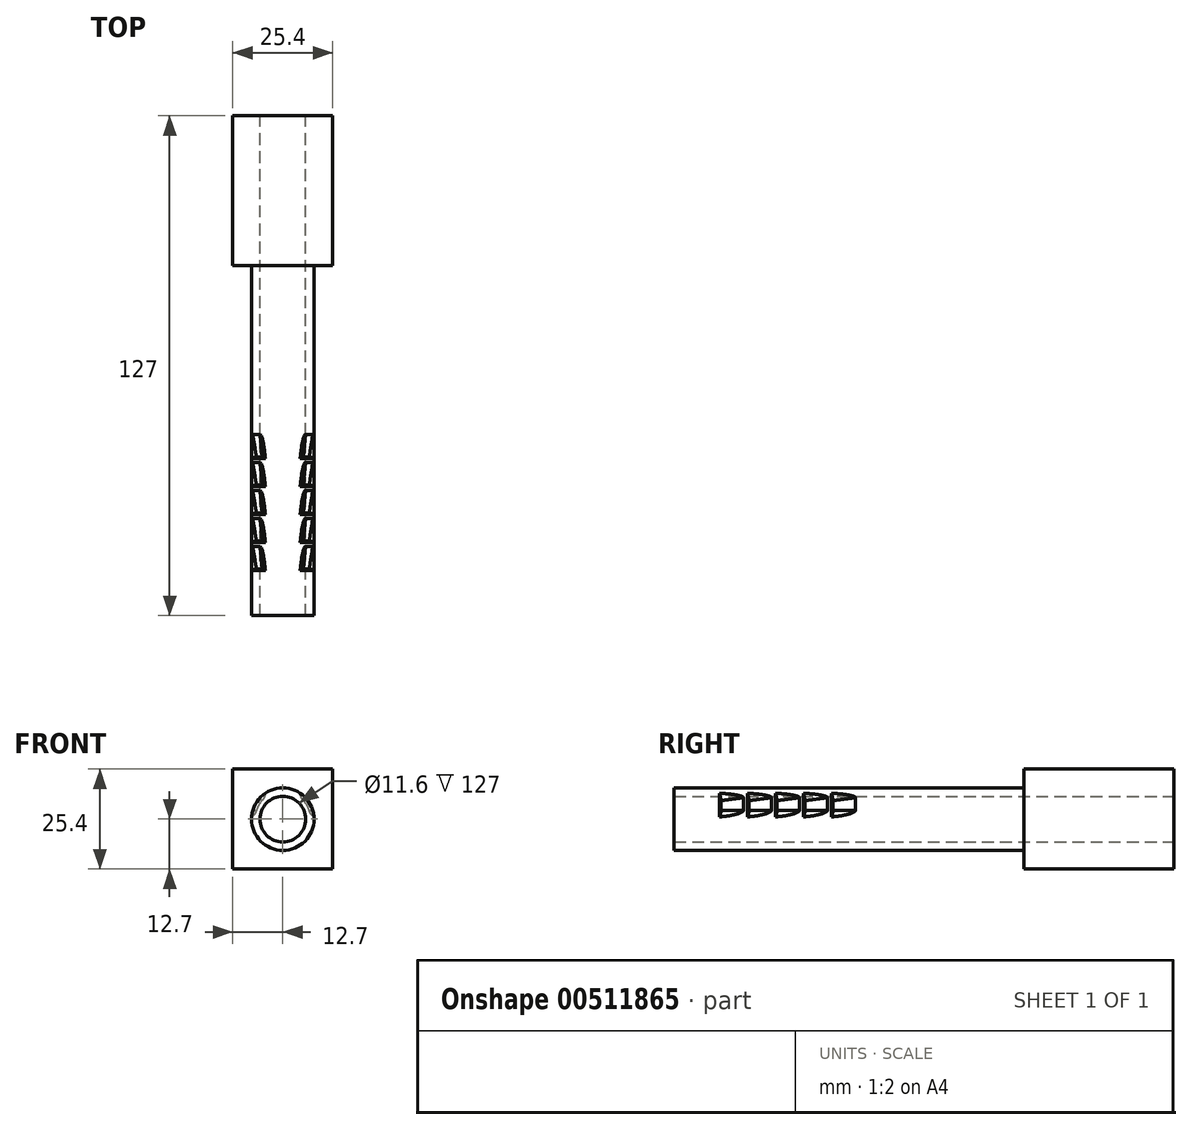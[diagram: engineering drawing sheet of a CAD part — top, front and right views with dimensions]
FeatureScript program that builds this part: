
annotation { "Feature Type Name" : "Feature", "Feature Type Description" : "" }
export const myFeature = defineFeature(function(context is Context, id is Id, definition is map)
    precondition{}
    {
        {
            var Q0;
            Q0=qCreatedBy(makeId("Front.planeOp"),FACE);
            var sketch = newSketch(context, id + "F0", { "sketchPlane" : qUnion([Q0])});
            skLineSegment(sketch, "E0.bottom", {"start": v(12.7, -12.7) * mm, "end": v(-12.7, -12.7) * mm});
            skLineSegment(sketch, "E0.top", {"start": v(12.7, 12.7) * mm, "end": v(-12.7, 12.7) * mm});
            skLineSegment(sketch, "E0.left", {"start": v(12.7, -12.7) * mm, "end": v(12.7, 12.7) * mm});
            skLineSegment(sketch, "E0.right", {"start": v(-12.7, -12.7) * mm, "end": v(-12.7, 12.7) * mm});
            skPoint(sketch, "E0.middle", {"position": v(0, 0) * mm});
            skCircle(sketch, "E1", {"center": v(0, 0) * mm, "radius": 7.94 * mm});
            skCircle(sketch, "E2", {"center": v(0, 0) * mm, "radius": 5.8 * mm});
            skSolve(sketch);
        }
        {
            var Q0;
            Q0=qSketchRegion(id+"F0",true);
            var Q1;
            Q1=makeQuery(id+"F0.imprint","IMPRINT",FACE,{"disambiguationData":[TD([[makeQuery(id+"F0.imprint","IMPRINT",EDGE,{"derivedFrom":sQuery(id+"F0.wireOp",EDGE,"E1")}),1.0]])]});
            extrude(context, id + "F1", {"entities" : qUnion([Q0, Q1]), "depth" : 38.1 * mm});
        }
        {
            var Q0;
            Q0=makeQuery(id+"F0.imprint","IMPRINT",FACE,{"disambiguationData":[TD([[makeQuery(id+"F0.imprint","IMPRINT",EDGE,{"derivedFrom":sQuery(id+"F0.wireOp",EDGE,"E1")}),1.0]])]});
            extrude(context, id + "F2", {"entities" : qUnion([Q0]), "operationType" : NewBodyOperationType.ADD, "depth" : 127 * mm, "offsetDistance" : 25.4 * mm});
        }
        {
            var Q0;
            Q0=qCreatedBy(makeId("Top.planeOp"),FACE);
            var sketch = newSketch(context, id + "F3", { "sketchPlane" : qUnion([Q0])});
            skLineSegment(sketch, "E3", {"start": v(-8.1, -115.62) * mm, "end": v(-7.07, -115.1) * mm});
            skLineSegment(sketch, "E4", {"start": v(-7.07, -115.1) * mm, "end": v(-8.03, -108.82) * mm});
            skLineSegment(sketch, "E5", {"start": v(-8.03, -108.82) * mm, "end": v(-8.1, -115.62) * mm});
            skLineSegment(sketch, "E6.0.1.0", {"start": v(-8.03, -101.7) * mm, "end": v(-8.1, -108.5) * mm});
            skLineSegment(sketch, "E6.0.1.1", {"start": v(-7.07, -108) * mm, "end": v(-8.03, -101.7) * mm});
            skLineSegment(sketch, "E6.0.1.2", {"start": v(-8.1, -108.5) * mm, "end": v(-7.07, -108) * mm});
            skLineSegment(sketch, "E6.0.2.0", {"start": v(-8.03, -94.6) * mm, "end": v(-8.1, -101.4) * mm});
            skLineSegment(sketch, "E6.0.2.1", {"start": v(-7.07, -100.88) * mm, "end": v(-8.03, -94.6) * mm});
            skLineSegment(sketch, "E6.0.2.2", {"start": v(-8.1, -101.4) * mm, "end": v(-7.07, -100.88) * mm});
            skLineSegment(sketch, "E6.0.3.0", {"start": v(-8.03, -87.48) * mm, "end": v(-8.1, -94.28) * mm});
            skLineSegment(sketch, "E6.0.3.1", {"start": v(-7.07, -93.77) * mm, "end": v(-8.03, -87.48) * mm});
            skLineSegment(sketch, "E6.0.3.2", {"start": v(-8.1, -94.28) * mm, "end": v(-7.07, -93.77) * mm});
            skLineSegment(sketch, "E6.0.4.0", {"start": v(-8.03, -80.37) * mm, "end": v(-8.1, -87.17) * mm});
            skLineSegment(sketch, "E6.0.4.1", {"start": v(-7.07, -86.66) * mm, "end": v(-8.03, -80.37) * mm});
            skLineSegment(sketch, "E6.0.4.2", {"start": v(-8.1, -87.17) * mm, "end": v(-7.07, -86.66) * mm});
            skLineSegment(sketch, "E6.direction1", {"start": v(-8.1, -115.62) * mm, "end": v(-0.22, -115.62) * mm, "construction": true});
            skLineSegment(sketch, "E6.direction2", {"start": v(-8.1, -115.62) * mm, "end": v(-8.1, -108.5) * mm, "construction": true});
            skSolve(sketch);
        }
        {
            var Q0;
            Q0 = qSketchRegion(id + "F3", true);
            var Q1;
            Q1=makeQuery(id+"F1.opExtrude","CAP_EDGE",EDGE,{"disambiguationData":[OSD([sQuery(id+"F0.wireOp",EDGE,"E2")])],"isStart":true});
            revolve(context, id + "F4", {"operationType" : NewBodyOperationType.REMOVE, "entities" : qUnion([Q0]), "axis" : qUnion([Q1]), "revolveType" : RevolveType.ONE_DIRECTION, "oppositeDirection" : true, "angle" : 60 * degree});
        }
        {
            var Q0;
            Q0 = qSketchRegion(id + "F3", true);
            var Q1;
            Q1=makeQuery(id+"F2.opExtrude","SWEPT_FACE",FACE,{"disambiguationData":[OSD([sQuery(id+"F0.wireOp",EDGE,"E1")])]});
            revolve(context, id + "F5", {"operationType" : NewBodyOperationType.REMOVE, "entities" : qUnion([Q0]), "axis" : qUnion([Q1]), "revolveType" : RevolveType.TWO_DIRECTIONS, "angle" : 180 * degree, "angleBack" : 120 * degree});
        }
        {
            var Q0;
            Q0=makeQuery(id+"F5.boolean.opBoolean","COPY",EDGE,{"derivedFrom":makeQuery(id+"F5.opRevolve","CAP_EDGE",EDGE,{"disambiguationData":[OSD([sQuery(id+"F3.wireOp",EDGE,"E4")])],"isStart":true})});
            var Q1;
            Q1=makeQuery(id+"F5.boolean.opBoolean","COPY",EDGE,{"derivedFrom":makeQuery(id+"F5.opRevolve","CAP_EDGE",EDGE,{"disambiguationData":[OSD([sQuery(id+"F3.wireOp",EDGE,"E4")])],"isStart":false})});
            var Q2;
            Q2=makeQuery(id+"F5.boolean.opBoolean","COPY",EDGE,{"derivedFrom":makeQuery(id+"F5.opRevolve","CAP_EDGE",EDGE,{"disambiguationData":[OSD([sQuery(id+"F3.wireOp",EDGE,"E6.0.1.1")])],"isStart":true})});
            var Q3;
            Q3=makeQuery(id+"F5.boolean.opBoolean","COPY",EDGE,{"derivedFrom":makeQuery(id+"F5.opRevolve","CAP_EDGE",EDGE,{"disambiguationData":[OSD([sQuery(id+"F3.wireOp",EDGE,"E6.0.1.1")])],"isStart":false})});
            var Q4;
            Q4=makeQuery(id+"F5.boolean.opBoolean","COPY",EDGE,{"derivedFrom":makeQuery(id+"F5.opRevolve","CAP_EDGE",EDGE,{"disambiguationData":[OSD([sQuery(id+"F3.wireOp",EDGE,"E6.0.2.1")])],"isStart":true})});
            var Q5;
            Q5=makeQuery(id+"F5.boolean.opBoolean","COPY",EDGE,{"derivedFrom":makeQuery(id+"F5.opRevolve","CAP_EDGE",EDGE,{"disambiguationData":[OSD([sQuery(id+"F3.wireOp",EDGE,"E6.0.2.1")])],"isStart":false})});
            var Q6;
            Q6=makeQuery(id+"F5.boolean.opBoolean","COPY",EDGE,{"derivedFrom":makeQuery(id+"F5.opRevolve","CAP_EDGE",EDGE,{"disambiguationData":[OSD([sQuery(id+"F3.wireOp",EDGE,"E6.0.3.1")])],"isStart":false})});
            var Q7;
            Q7=makeQuery(id+"F5.boolean.opBoolean","COPY",EDGE,{"derivedFrom":makeQuery(id+"F5.opRevolve","CAP_EDGE",EDGE,{"disambiguationData":[OSD([sQuery(id+"F3.wireOp",EDGE,"E6.0.3.1")])],"isStart":true})});
            var Q8;
            Q8=makeQuery(id+"F5.boolean.opBoolean","COPY",EDGE,{"derivedFrom":makeQuery(id+"F5.opRevolve","CAP_EDGE",EDGE,{"disambiguationData":[OSD([sQuery(id+"F3.wireOp",EDGE,"E6.0.4.1")])],"isStart":true})});
            var Q9;
            Q9=makeQuery(id+"F5.boolean.opBoolean","COPY",EDGE,{"derivedFrom":makeQuery(id+"F5.opRevolve","CAP_EDGE",EDGE,{"disambiguationData":[OSD([sQuery(id+"F3.wireOp",EDGE,"E6.0.4.1")])],"isStart":false})});
            var Q10;
            Q10=makeQuery(id+"F4.boolean.opBoolean","COPY",EDGE,{"derivedFrom":makeQuery(id+"F4.opRevolve","CAP_EDGE",EDGE,{"disambiguationData":[OSD([sQuery(id+"F3.wireOp",EDGE,"E4")])],"isStart":false})});
            var Q11;
            Q11=makeQuery(id+"F4.boolean.opBoolean","COPY",EDGE,{"derivedFrom":makeQuery(id+"F4.opRevolve","CAP_EDGE",EDGE,{"disambiguationData":[OSD([sQuery(id+"F3.wireOp",EDGE,"E4")])],"isStart":true})});
            var Q12;
            Q12=makeQuery(id+"F4.boolean.opBoolean","COPY",EDGE,{"derivedFrom":makeQuery(id+"F4.opRevolve","CAP_EDGE",EDGE,{"disambiguationData":[OSD([sQuery(id+"F3.wireOp",EDGE,"E6.0.1.1")])],"isStart":true})});
            var Q13;
            Q13=makeQuery(id+"F4.boolean.opBoolean","COPY",EDGE,{"derivedFrom":makeQuery(id+"F4.opRevolve","CAP_EDGE",EDGE,{"disambiguationData":[OSD([sQuery(id+"F3.wireOp",EDGE,"E6.0.1.1")])],"isStart":false})});
            var Q14;
            Q14=makeQuery(id+"F4.boolean.opBoolean","COPY",EDGE,{"derivedFrom":makeQuery(id+"F4.opRevolve","CAP_EDGE",EDGE,{"disambiguationData":[OSD([sQuery(id+"F3.wireOp",EDGE,"E6.0.2.1")])],"isStart":false})});
            var Q15;
            Q15=makeQuery(id+"F4.boolean.opBoolean","COPY",EDGE,{"derivedFrom":makeQuery(id+"F4.opRevolve","CAP_EDGE",EDGE,{"disambiguationData":[OSD([sQuery(id+"F3.wireOp",EDGE,"E6.0.2.1")])],"isStart":true})});
            var Q16;
            Q16=makeQuery(id+"F4.boolean.opBoolean","COPY",EDGE,{"derivedFrom":makeQuery(id+"F4.opRevolve","CAP_EDGE",EDGE,{"disambiguationData":[OSD([sQuery(id+"F3.wireOp",EDGE,"E6.0.3.1")])],"isStart":false})});
            var Q17;
            Q17=makeQuery(id+"F4.boolean.opBoolean","COPY",EDGE,{"derivedFrom":makeQuery(id+"F4.opRevolve","CAP_EDGE",EDGE,{"disambiguationData":[OSD([sQuery(id+"F3.wireOp",EDGE,"E6.0.3.1")])],"isStart":true})});
            var Q18;
            Q18=makeQuery(id+"F4.boolean.opBoolean","COPY",EDGE,{"derivedFrom":makeQuery(id+"F4.opRevolve","CAP_EDGE",EDGE,{"disambiguationData":[OSD([sQuery(id+"F3.wireOp",EDGE,"E6.0.4.1")])],"isStart":false})});
            var Q19;
            Q19=makeQuery(id+"F4.boolean.opBoolean","COPY",EDGE,{"derivedFrom":makeQuery(id+"F4.opRevolve","CAP_EDGE",EDGE,{"disambiguationData":[OSD([sQuery(id+"F3.wireOp",EDGE,"E6.0.4.1")])],"isStart":true})});
            fillet(context, id + "F6", {"entities" : qUnion([Q0, Q1, Q2, Q3, Q4, Q5, Q6, Q7, Q8, Q9, Q10, Q11, Q12, Q13, Q14, Q15, Q16, Q17, Q18, Q19]), "radius" : 3.17 * mm, "tangentPropagation" : true, "allowEdgeOverflow" : false});
        }
    });
